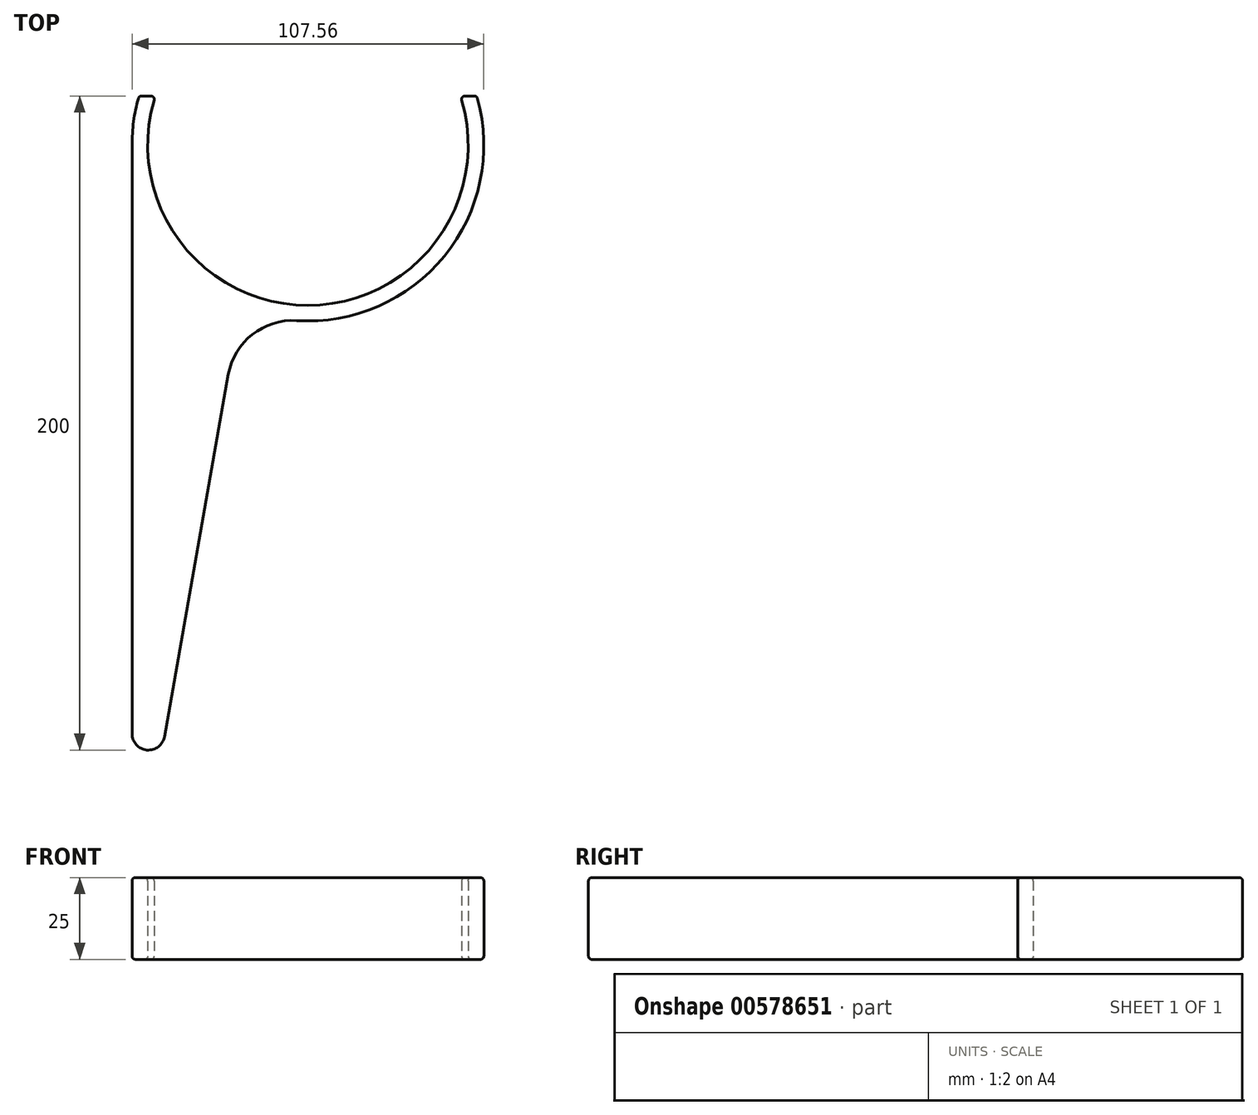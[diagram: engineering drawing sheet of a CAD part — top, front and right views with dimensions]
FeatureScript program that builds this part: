
annotation { "Feature Type Name" : "Feature", "Feature Type Description" : "" }
export const myFeature = defineFeature(function(context is Context, id is Id, definition is map)
    precondition{}
    {
        {
            var Q0;
            Q0=qCreatedBy(makeId("Top.planeOp"),FACE);
            var sketch = newSketch(context, id + "F0", { "sketchPlane" : qUnion([Q0])});
            skLineSegment(sketch, "E0", {"start": v(0, 57.15) * mm, "end": v(0, 237.15) * mm});
            skLineSegment(sketch, "E1", {"start": v(0, 237.15) * mm, "end": v(0, 57.15) * mm});
            skLineSegment(sketch, "E2", {"start": v(29.44, 166.99) * mm, "end": v(9.92, 56.28) * mm});
            skArc(sketch, "E3", {"start": v(2.13, 252.15) * mm, "mid": v(0.54, 244.73) * mm, "end": v(0, 237.15) * mm});
            skArc(sketch, "E4", {"start": v(7.13, 252.15) * mm, "mid": v(53.78, 188.15) * mm, "end": v(100.43, 252.15) * mm});
            skLineSegment(sketch, "E5", {"start": v(2.13, 252.15) * mm, "end": v(7.13, 252.15) * mm});
            skLineSegment(sketch, "E6", {"start": v(100.43, 252.15) * mm, "end": v(105.43, 252.15) * mm});
            skLineSegment(sketch, "E7", {"start": v(7.13, 252.15) * mm, "end": v(100.43, 252.15) * mm, "construction": true});
            skArc(sketch, "E8.trimOffspring", {"start": v(50.4, 183.48) * mm, "mid": v(95.75, 203.52) * mm, "end": v(105.43, 252.15) * mm});
            skPoint(sketch, "E9.visualSharp", {"position": v(33.06, 187.52) * mm});
            skArc(sketch, "E9.filletArc", {"start": v(50.4, 183.48) * mm, "mid": v(36.77, 179.23) * mm, "end": v(29.44, 166.99) * mm});
            skArc(sketch, "E10", {"start": v(100.43, 252.15) * mm, "mid": v(53.78, 286.15) * mm, "end": v(7.13, 252.15) * mm, "construction": true});
            skPoint(sketch, "E11.visualSharp", {"position": v(0, 0) * mm});
            skArc(sketch, "E11.filletArc", {"start": v(0, 57.15) * mm, "mid": v(4.56, 52.17) * mm, "end": v(9.92, 56.28) * mm});
            skLineSegment(sketch, "E12", {"start": v(0, 57.15) * mm, "end": v(0, 52.15) * mm, "construction": true});
            skLineSegment(sketch, "E13", {"start": v(0, 52.15) * mm, "end": v(0, 52.15) * mm});
            skLineSegment(sketch, "E14", {"start": v(5, 52.15) * mm, "end": v(0, 52.15) * mm, "construction": true});
            skSolve(sketch);
        }
        {
            var Q0;
            Q0 = qSketchRegion(id + "F0", true);
            extrude(context, id + "F1", {"entities" : qUnion([Q0]), "depth" : 25 * mm, "offsetDistance" : 25 * mm});
        }
        {
            var Q0;
            Q0=makeQuery(id+"F1.opExtrude","CAP_EDGE",EDGE,{"disambiguationData":[OSD([sQuery(id+"F0.wireOp",EDGE,"E2")])],"isStart":false});
            var Q1;
            Q1=makeQuery(id+"F1.opExtrude","CAP_EDGE",EDGE,{"disambiguationData":[OSD([sQuery(id+"F0.wireOp",EDGE,"E6")])],"isStart":false});
            var Q2;
            Q2=makeQuery(id+"F1.opExtrude","CAP_EDGE",EDGE,{"disambiguationData":[OSD([sQuery(id+"F0.wireOp",EDGE,"E4")])],"isStart":false});
            var Q3;
            Q3=makeQuery(id+"F1.opExtrude","CAP_EDGE",EDGE,{"disambiguationData":[OSD([sQuery(id+"F0.wireOp",EDGE,"E5")])],"isStart":false});
            var Q4;
            Q4=makeQuery(id+"F1.opExtrude","CAP_EDGE",EDGE,{"disambiguationData":[OSD([sQuery(id+"F0.wireOp",EDGE,"E3")])],"isStart":false});
            var Q5;
            Q5=makeQuery(id+"F1.opExtrude","CAP_EDGE",EDGE,{"disambiguationData":[OSD([sQuery(id+"F0.wireOp",EDGE,"E2")])],"isStart":true});
            var Q6;
            Q6=makeQuery(id+"F1.opExtrude","CAP_EDGE",EDGE,{"disambiguationData":[OSD([sQuery(id+"F0.wireOp",EDGE,"E9.filletArc")])],"isStart":true});
            var Q7;
            Q7=makeQuery(id+"F1.opExtrude","CAP_EDGE",EDGE,{"disambiguationData":[OSD([sQuery(id+"F0.wireOp",EDGE,"E8.trimOffspring")])],"isStart":true});
            var Q8;
            Q8=makeQuery(id+"F1.opExtrude","CAP_EDGE",EDGE,{"disambiguationData":[OSD([sQuery(id+"F0.wireOp",EDGE,"E9.filletArc")])],"isStart":false});
            var Q9;
            Q9=makeQuery(id+"F1.opExtrude","CAP_EDGE",EDGE,{"disambiguationData":[OSD([sQuery(id+"F0.wireOp",EDGE,"E8.trimOffspring")])],"isStart":false});
            var Q10;
            Q10=makeQuery(id+"F1.opExtrude","CAP_EDGE",EDGE,{"disambiguationData":[OSD([sQuery(id+"F0.wireOp",EDGE,"E6")])],"isStart":true});
            var Q11;
            Q11=makeQuery(id+"F1.opExtrude","CAP_EDGE",EDGE,{"disambiguationData":[OSD([sQuery(id+"F0.wireOp",EDGE,"E4")])],"isStart":true});
            var Q12;
            Q12=makeQuery(id+"F1.opExtrude","CAP_EDGE",EDGE,{"disambiguationData":[OSD([sQuery(id+"F0.wireOp",EDGE,"E1")])],"isStart":true});
            var Q13;
            Q13=makeQuery(id+"F1.opExtrude","CAP_FACE",FACE,{"disambiguationData":[OSD([sQuery(id+"F0.wireOp",EDGE,"E1"),sQuery(id+"F0.wireOp",EDGE,"E2"),sQuery(id+"F0.wireOp",EDGE,"E3"),sQuery(id+"F0.wireOp",EDGE,"E4"),sQuery(id+"F0.wireOp",EDGE,"E5"),sQuery(id+"F0.wireOp",EDGE,"E6"),sQuery(id+"F0.wireOp",EDGE,"E8.trimOffspring"),sQuery(id+"F0.wireOp",EDGE,"E9.filletArc")])],"isStart":true});
            var Q14;
            Q14=makeQuery(id+"F1.opExtrude","CAP_EDGE",EDGE,{"disambiguationData":[OSD([sQuery(id+"F0.wireOp",EDGE,"E5")])],"isStart":true});
            var Q15;
            Q15=makeQuery(id+"F1.opExtrude","SWEPT_EDGE",EDGE,{"disambiguationData":[OSD([sQuery(id+"F0.wireOp",EDGE,"E6"),sQuery(id+"F0.wireOp",EDGE,"E8.trimOffspring")])]});
            var Q16;
            Q16=makeQuery(id+"F1.opExtrude","SWEPT_EDGE",EDGE,{"disambiguationData":[OSD([sQuery(id+"F0.wireOp",EDGE,"E4"),sQuery(id+"F0.wireOp",EDGE,"E6")])]});
            var Q17;
            Q17=makeQuery(id+"F1.opExtrude","SWEPT_EDGE",EDGE,{"disambiguationData":[OSD([sQuery(id+"F0.wireOp",EDGE,"E4"),sQuery(id+"F0.wireOp",EDGE,"E5")])]});
            var Q18;
            Q18=makeQuery(id+"F1.opExtrude","SWEPT_EDGE",EDGE,{"disambiguationData":[OSD([sQuery(id+"F0.wireOp",EDGE,"E3"),sQuery(id+"F0.wireOp",EDGE,"E5")])]});
            var Q19;
            Q19=makeQuery(id+"F1.opExtrude","SWEPT_EDGE",EDGE,{"disambiguationData":[OSD([sQuery(id+"F0.wireOp",EDGE,"E1"),sQuery(id+"F0.wireOp",EDGE,"E2")])]});
            fillet(context, id + "F2", {"entities" : qUnion([Q0, Q1, Q2, Q3, Q4, Q5, Q6, Q7, Q8, Q9, Q10, Q11, Q12, Q13, Q14, Q15, Q16, Q17, Q18, Q19]), "radius" : 1 * mm, "tangentPropagation" : true, "allowEdgeOverflow" : false});
        }
    });
